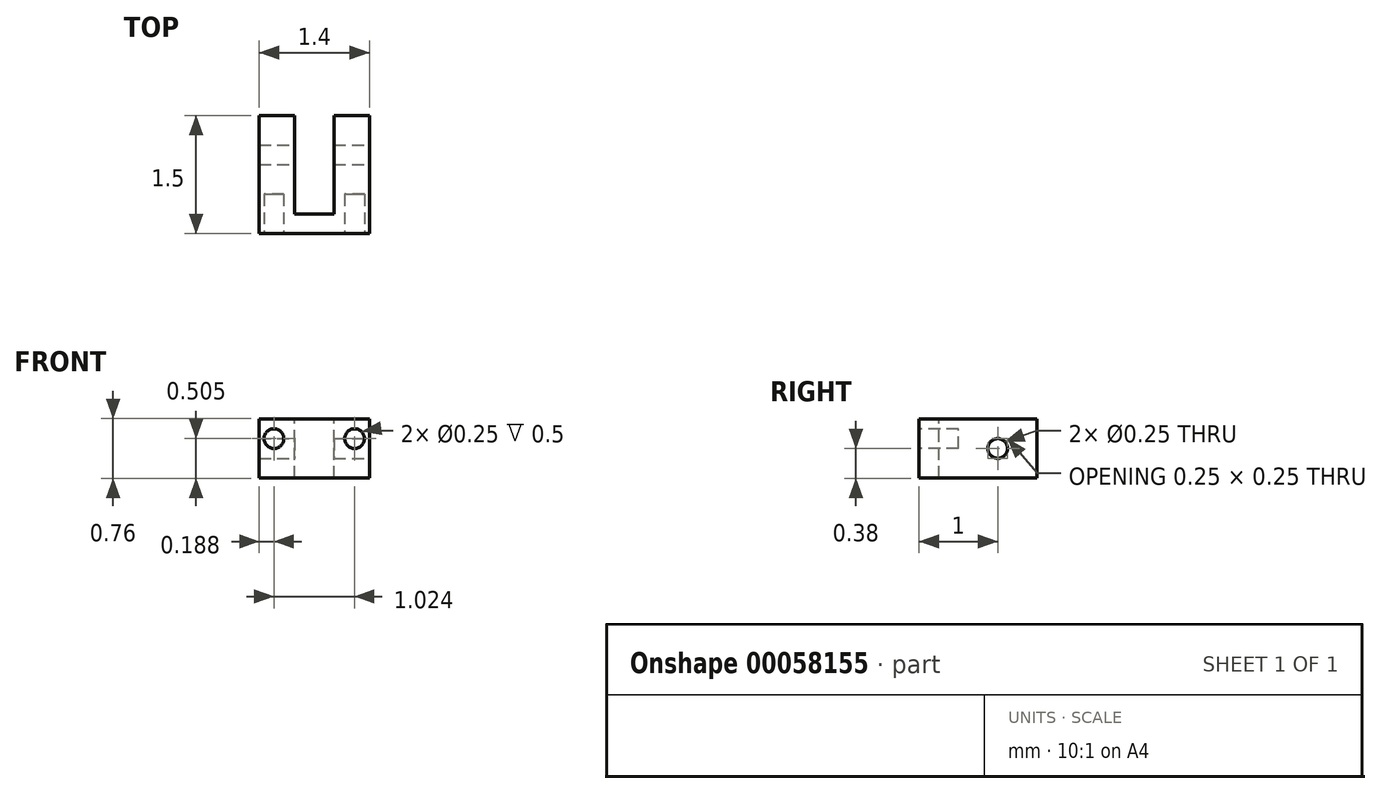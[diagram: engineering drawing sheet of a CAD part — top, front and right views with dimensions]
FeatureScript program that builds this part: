
annotation { "Feature Type Name" : "Feature", "Feature Type Description" : "" }
export const myFeature = defineFeature(function(context is Context, id is Id, definition is map)
    precondition{}
    {
        {
            var Q0;
            Q0=qCreatedBy(makeId("Front.planeOp"),FACE);
            var sketch = newSketch(context, id + "F0", { "sketchPlane" : qUnion([Q0])});
            skLineSegment(sketch, "E0.rect.bottom", {"start": v(0.7, 0.37) * mm, "end": v(-0.7, 0.37) * mm});
            skLineSegment(sketch, "E0.rect.top", {"start": v(0.7, -0.38) * mm, "end": v(-0.7, -0.38) * mm});
            skLineSegment(sketch, "E0.rect.left", {"start": v(0.7, 0.37) * mm, "end": v(0.7, -0.38) * mm});
            skLineSegment(sketch, "E0.rect.right", {"start": v(-0.7, 0.37) * mm, "end": v(-0.7, -0.38) * mm});
            skPoint(sketch, "E0.rect.middle", {"position": v(0, 0) * mm});
            skSolve(sketch);
        }
        {
            var Q0;
            Q0 = qSketchRegion(id + "F0", true);
            extrude(context, id + "F1", {"entities" : qUnion([Q0]), "endBound" : BoundingType.SYMMETRIC, "depth" : 1.5 * mm});
        }
        {
            var Q0;
            Q0=makeQuery(id+"F1.opExtrude","SWEPT_FACE",FACE,{"disambiguationData":[OSD([sQuery(id+"F0.wireOp",EDGE,"E0.rect.left")])]});
            var sketch = newSketch(context, id + "F2", { "sketchPlane" : qUnion([Q0])});
            skCircle(sketch, "E1", {"center": v(0.25, 0) * mm, "radius": 0.12 * mm});
            skSolve(sketch);
        }
        {
            var Q0;
            Q0 = qSketchRegion(id + "F2", true);
            extrude(context, id + "F3", {"entities" : qUnion([Q0]), "operationType" : NewBodyOperationType.REMOVE, "oppositeDirection" : true, "depth" : 25 * mm});
        }
        {
            var Q0;
            Q0=makeQuery(id+"F1.opExtrude","SWEPT_FACE",FACE,{"disambiguationData":[OSD([sQuery(id+"F0.wireOp",EDGE,"E0.rect.bottom")])]});
            var sketch = newSketch(context, id + "F4", { "sketchPlane" : qUnion([Q0])});
            skLineSegment(sketch, "E2.bottom", {"start": v(-0.25, 0.75) * mm, "end": v(0.25, 0.75) * mm});
            skLineSegment(sketch, "E2.top", {"start": v(-0.25, -0.5) * mm, "end": v(0.25, -0.5) * mm});
            skLineSegment(sketch, "E2.left", {"start": v(-0.25, 0.75) * mm, "end": v(-0.25, -0.5) * mm});
            skLineSegment(sketch, "E2.right", {"start": v(0.25, 0.75) * mm, "end": v(0.25, -0.5) * mm});
            skSolve(sketch);
        }
        {
            var Q0;
            Q0 = qSketchRegion(id + "F4", true);
            extrude(context, id + "F5", {"entities" : qUnion([Q0]), "operationType" : NewBodyOperationType.REMOVE, "endBound" : BoundingType.SYMMETRIC, "oppositeDirection" : true, "depth" : 25 * mm});
        }
        {
            var Q0;
            Q0=makeQuery(id+"F1.opExtrude","CAP_FACE",FACE,{"disambiguationData":[OSD([sQuery(id+"F0.wireOp",EDGE,"E0.rect.bottom"),sQuery(id+"F0.wireOp",EDGE,"E0.rect.top"),sQuery(id+"F0.wireOp",EDGE,"E0.rect.left"),sQuery(id+"F0.wireOp",EDGE,"E0.rect.right")])],"isStart":false});
            var sketch = newSketch(context, id + "F6", { "sketchPlane" : qUnion([Q0])});
            skCircle(sketch, "E3", {"center": v(0.51, 0.12) * mm, "radius": 0.12 * mm});
            skCircle(sketch, "E4", {"center": v(-0.51, 0.12) * mm, "radius": 0.12 * mm});
            skSolve(sketch);
        }
        {
            var Q0;
            Q0 = qSketchRegion(id + "F6", true);
            extrude(context, id + "F7", {"entities" : qUnion([Q0]), "operationType" : NewBodyOperationType.REMOVE, "oppositeDirection" : true, "depth" : 0.5 * mm});
        }
    });
